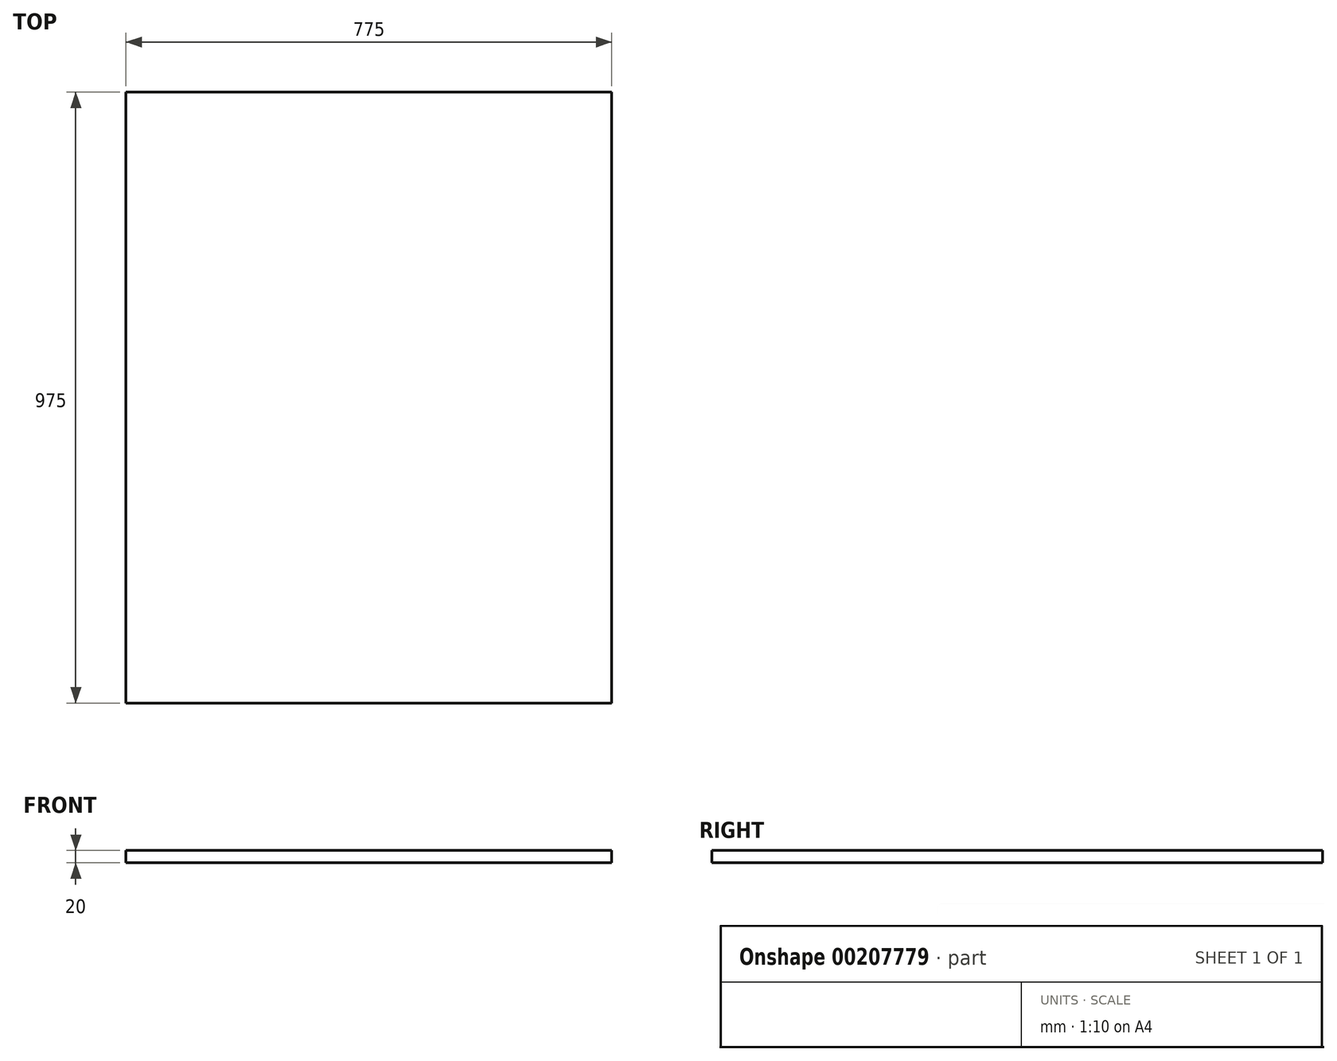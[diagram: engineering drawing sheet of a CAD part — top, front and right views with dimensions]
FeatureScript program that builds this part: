
annotation { "Feature Type Name" : "Feature", "Feature Type Description" : "" }
export const myFeature = defineFeature(function(context is Context, id is Id, definition is map)
    precondition{}
    {
        {
            var Q0;
            Q0=qCreatedBy(makeId("Top.planeOp"),FACE);
            var sketch = newSketch(context, id + "F0", { "sketchPlane" : qUnion([Q0])});
            skLineSegment(sketch, "E0.bottom", {"start": v(0, 0) * mm, "end": v(-775, 0) * mm});
            skLineSegment(sketch, "E0.top", {"start": v(0, 975) * mm, "end": v(-775, 975) * mm});
            skLineSegment(sketch, "E0.left", {"start": v(0, 0) * mm, "end": v(0, 975) * mm});
            skLineSegment(sketch, "E0.right", {"start": v(-775, 0) * mm, "end": v(-775, 975) * mm});
            skSolve(sketch);
        }
        {
            var Q0;
            Q0=makeQuery(id+"F0.imprint","IMPRINT",FACE,{"disambiguationData":[TD([[makeQuery(id+"F0.imprint","IMPRINT",EDGE,{"derivedFrom":sQuery(id+"F0.wireOp",EDGE,"E0.bottom")}),-1.0]])]});
            extrude(context, id + "F1", {"entities" : qUnion([Q0]), "depth" : 20 * mm});
        }
    });
